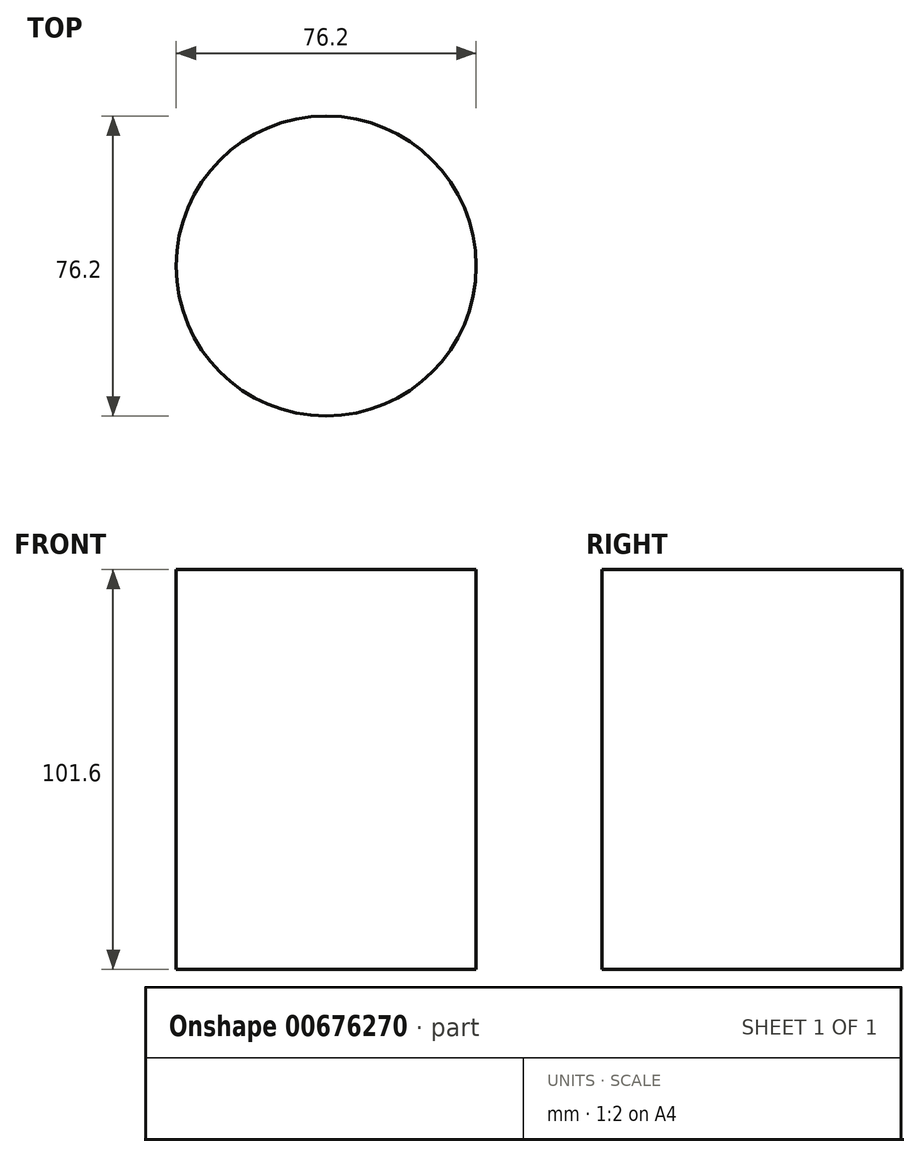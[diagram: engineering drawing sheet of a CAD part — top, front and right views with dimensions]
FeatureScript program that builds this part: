
annotation { "Feature Type Name" : "Feature", "Feature Type Description" : "" }
export const myFeature = defineFeature(function(context is Context, id is Id, definition is map)
    precondition{}
    {
        {
            var Q0;
            Q0=qCreatedBy(makeId("Top.planeOp"),FACE);
            var sketch = newSketch(context, id + "F0", { "sketchPlane" : qUnion([Q0])});
            skCircle(sketch, "E0", {"center": v(0, 0) * mm, "radius": 38.1 * mm});
            skSolve(sketch);
        }
        {
            var Q0;
            Q0=makeQuery(id+"F0.imprint","IMPRINT",FACE,{"disambiguationData":[TD([[makeQuery(id+"F0.imprint","IMPRINT",EDGE,{"derivedFrom":sQuery(id+"F0.wireOp",EDGE,"E0")}),1.0]])]});
            extrude(context, id + "F1", {"entities" : qUnion([Q0]), "depth" : 101.6 * mm, "offsetDistance" : 25.4 * mm});
        }
    });
